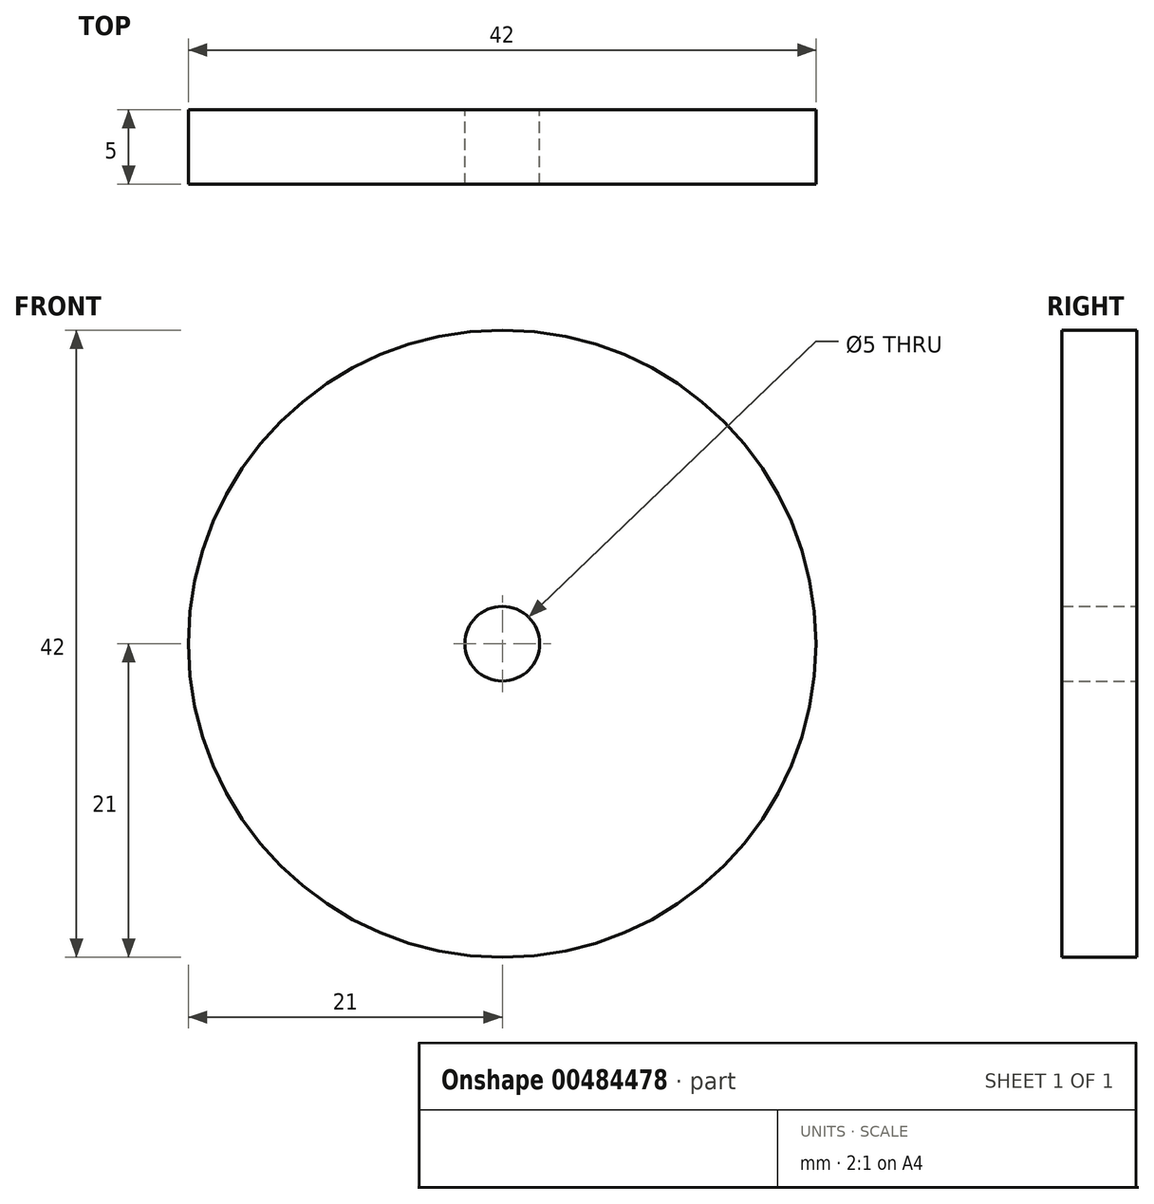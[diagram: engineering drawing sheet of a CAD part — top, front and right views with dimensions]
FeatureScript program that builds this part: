
annotation { "Feature Type Name" : "Feature", "Feature Type Description" : "" }
export const myFeature = defineFeature(function(context is Context, id is Id, definition is map)
    precondition{}
    {
        {
            var Q0;
            Q0=qCreatedBy(makeId("Front.planeOp"),FACE);
            var sketch = newSketch(context, id + "F0", { "sketchPlane" : qUnion([Q0])});
            skCircle(sketch, "E0", {"center": v(0, 0) * mm, "radius": 21 * mm});
            skCircle(sketch, "E1", {"center": v(0, 0) * mm, "radius": 2.5 * mm});
            skSolve(sketch);
        }
        {
            var Q0;
            Q0=makeQuery(id+"F0.imprint","IMPRINT",FACE,{"disambiguationData":[TD([[makeQuery(id+"F0.imprint","IMPRINT",EDGE,{"derivedFrom":sQuery(id+"F0.wireOp",EDGE,"E0")}),1.0]])]});
            var Q1;
            Q1=sQuery(id+"F0.wireOp",EDGE,"E0");
            extrude(context, id + "F1", {"entities" : qUnion([Q0]), "surfaceEntities" : qUnion([Q1]), "depth" : 5 * mm});
        }
    });
